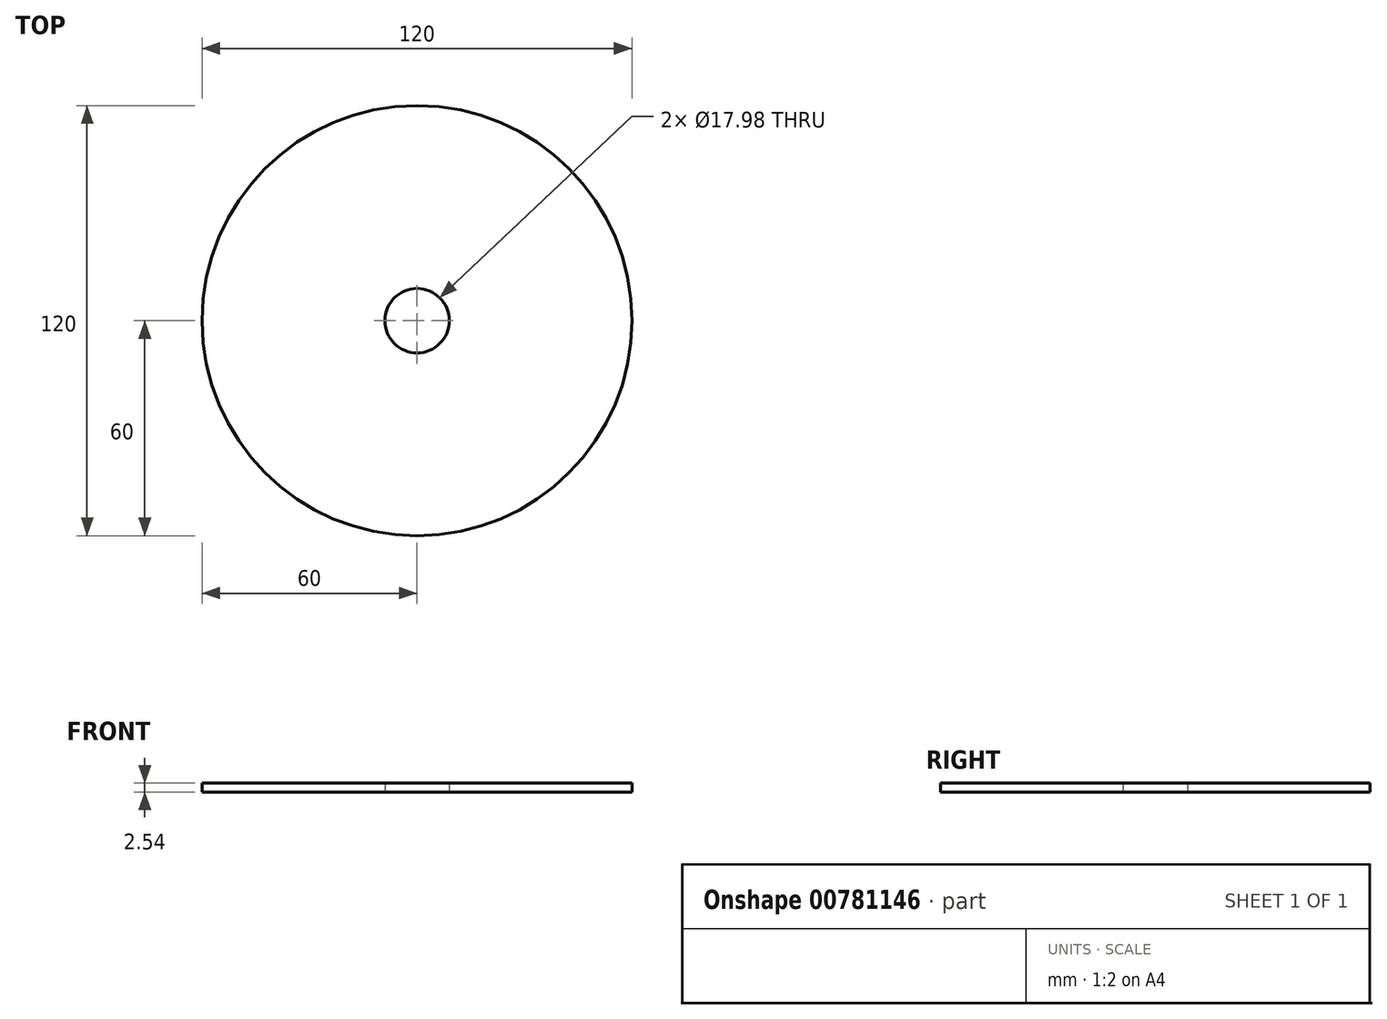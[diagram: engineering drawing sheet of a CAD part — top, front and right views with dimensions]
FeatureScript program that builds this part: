
annotation { "Feature Type Name" : "Feature", "Feature Type Description" : "" }
export const myFeature = defineFeature(function(context is Context, id is Id, definition is map)
    precondition{}
    {
        {
            var Q0;
            Q0=qCreatedBy(makeId("Top.planeOp"),FACE);
            var sketch = newSketch(context, id + "F0", { "sketchPlane" : qUnion([Q0])});
            skCircle(sketch, "E0", {"center": v(0, 0) * mm, "radius": 60 * mm});
            skCircle(sketch, "E1", {"center": v(0, 0) * mm, "radius": 9 * mm});
            skSolve(sketch);
        }
        {
            var Q0;
            Q0=makeQuery(id+"F0.imprint","IMPRINT",FACE,{"disambiguationData":[TD([[makeQuery(id+"F0.imprint","IMPRINT",EDGE,{"derivedFrom":sQuery(id+"F0.wireOp",EDGE,"E0")}),1.0]])]});
            extrude(context, id + "F1", {"entities" : qUnion([Q0]), "depth" : 2.54 * mm, "offsetDistance" : 25.4 * mm});
        }
    });
